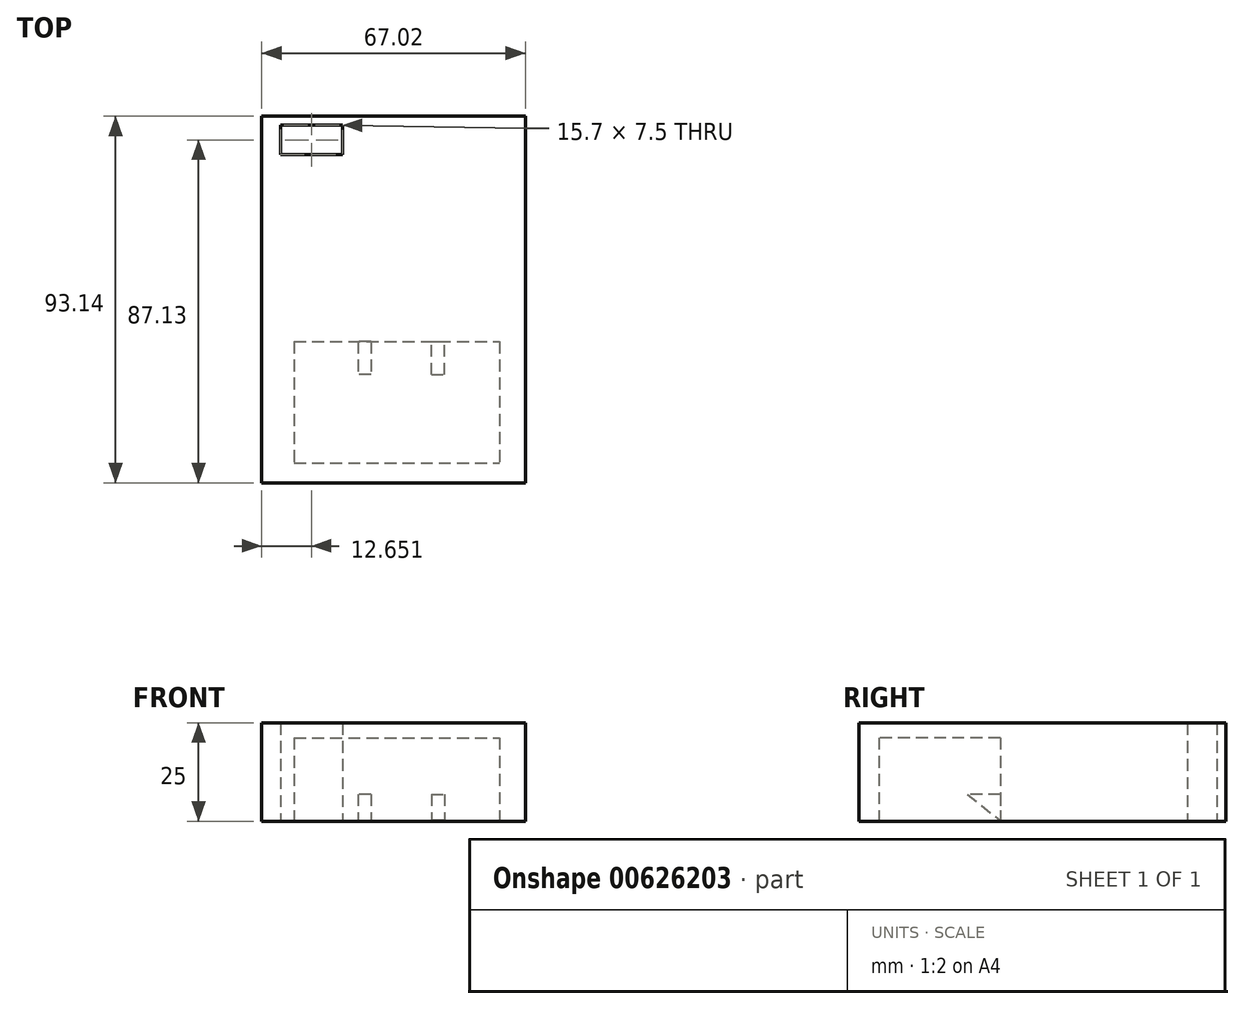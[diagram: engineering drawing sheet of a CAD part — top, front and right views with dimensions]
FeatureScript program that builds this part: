
annotation { "Feature Type Name" : "Feature", "Feature Type Description" : "" }
export const myFeature = defineFeature(function(context is Context, id is Id, definition is map)
    precondition{}
    {
        {
            var Q0;
            Q0=qCreatedBy(makeId("Top.planeOp"),FACE);
            var sketch = newSketch(context, id + "F0", { "sketchPlane" : qUnion([Q0])});
            skLineSegment(sketch, "E0.bottom", {"start": v(-46.4, 50.23) * mm, "end": v(20.62, 50.23) * mm});
            skLineSegment(sketch, "E0.top", {"start": v(-46.4, -42.9) * mm, "end": v(20.62, -42.9) * mm});
            skLineSegment(sketch, "E0.left", {"start": v(-46.4, 50.23) * mm, "end": v(-46.4, -3.55) * mm});
            skLineSegment(sketch, "E0.right", {"start": v(20.62, 50.23) * mm, "end": v(20.62, -3.86) * mm});
            skLineSegment(sketch, "E1", {"start": v(-46.4, -3.55) * mm, "end": v(-46.4, -42.9) * mm});
            skLineSegment(sketch, "E2", {"start": v(20.62, -3.86) * mm, "end": v(20.62, -42.9) * mm});
            skLineSegment(sketch, "E3", {"start": v(-46.4, -3.55) * mm, "end": v(20.62, -3.86) * mm});
            skSolve(sketch);
        }
        {
            var Q0;
            Q0=qCreatedBy(makeId("Top.planeOp"),FACE);
            var sketch = newSketch(context, id + "F1", { "sketchPlane" : qUnion([Q0])});
            skLineSegment(sketch, "E4.bottom", {"start": v(-41.6, 47.97) * mm, "end": v(-25.9, 47.97) * mm});
            skLineSegment(sketch, "E4.top", {"start": v(-41.6, 40.47) * mm, "end": v(-25.9, 40.47) * mm});
            skLineSegment(sketch, "E4.left", {"start": v(-41.6, 47.97) * mm, "end": v(-41.6, 40.47) * mm});
            skLineSegment(sketch, "E4.right", {"start": v(-25.9, 47.97) * mm, "end": v(-25.9, 40.47) * mm});
            skSolve(sketch);
        }
        {
            var Q0;
            Q0 = qSketchRegion(id + "F0", true);
            extrude(context, id + "F2", {"entities" : qUnion([Q0]), "depth" : 25 * mm, "offsetDistance" : 25 * mm});
        }
        {
            var Q0;
            Q0 = qSketchRegion(id + "F1", true);
            extrude(context, id + "F3", {"entities" : qUnion([Q0]), "operationType" : NewBodyOperationType.REMOVE, "depth" : 73 * mm, "offsetDistance" : 25 * mm});
        }
        {
            var Q0;
            Q0=qCreatedBy(makeId("Top.planeOp"),FACE);
            var sketch = newSketch(context, id + "F4", { "sketchPlane" : qUnion([Q0])});
            skLineSegment(sketch, "E5.bottom", {"start": v(-38.15, -7.01) * mm, "end": v(14.08, -7.01) * mm});
            skLineSegment(sketch, "E5.top", {"start": v(-38.15, -37.91) * mm, "end": v(14.08, -37.91) * mm});
            skLineSegment(sketch, "E5.left", {"start": v(-38.15, -7.01) * mm, "end": v(-38.15, -37.91) * mm});
            skLineSegment(sketch, "E5.right", {"start": v(14.08, -7.01) * mm, "end": v(14.08, -37.91) * mm});
            skSolve(sketch);
        }
        {
            var Q0;
            Q0 = qSketchRegion(id + "F4", true);
            extrude(context, id + "F5", {"entities" : qUnion([Q0]), "operationType" : NewBodyOperationType.REMOVE, "depth" : 21.2 * mm, "offsetDistance" : 25 * mm});
        }
        {
            var Q0;
            Q0=qCreatedBy(makeId("Right.planeOp"),FACE);
            var sketch = newSketch(context, id + "F6", { "sketchPlane" : qUnion([Q0])});
            skLineSegment(sketch, "E6", {"start": v(-6.72, 0) * mm, "end": v(-6.72, 6.88) * mm});
            skLineSegment(sketch, "E7", {"start": v(-6.72, 6.88) * mm, "end": v(-15.45, 6.88) * mm});
            skLineSegment(sketch, "E8", {"start": v(-15.45, 6.88) * mm, "end": v(-6.72, 0) * mm});
            skSolve(sketch);
        }
        {
            var Q0;
            Q0 = qSketchRegion(id + "F6", true);
            extrude(context, id + "F7", {"entities" : qUnion([Q0]), "operationType" : NewBodyOperationType.ADD, "oppositeDirection" : true, "depth" : 3.3 * mm, "offsetDistance" : 25 * mm});
        }
        {
            var Q0;
            Q0=qCreatedBy(makeId("Right.planeOp"),FACE);
            cPlane(context, id + "F8", {"entities" : qUnion([Q0]), "cplaneType" : CPlaneType.OFFSET, "offset" : 21.9 * mm, "oppositeDirection" : true, "width" : 150 * mm, "height" : 150 * mm});
        }
        {
            var Q0;
            Q0=qCreatedBy(id+"F8.planeOp",FACE);
            var sketch = newSketch(context, id + "F9", { "sketchPlane" : qUnion([Q0])});
            skLineSegment(sketch, "E9.0", {"start": v(-6.72, 0) * mm, "end": v(-6.72, 6.88) * mm});
            skLineSegment(sketch, "E9.1", {"start": v(-6.72, 6.88) * mm, "end": v(-15.45, 6.88) * mm});
            skLineSegment(sketch, "E9.2", {"start": v(-15.45, 6.88) * mm, "end": v(-6.72, 0) * mm});
            skSolve(sketch);
        }
        {
            var Q0;
            Q0 = qSketchRegion(id + "F9", true);
            extrude(context, id + "F10", {"entities" : qUnion([Q0]), "operationType" : NewBodyOperationType.ADD, "depth" : 3.3 * mm, "offsetDistance" : 25 * mm});
        }
    });
